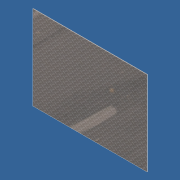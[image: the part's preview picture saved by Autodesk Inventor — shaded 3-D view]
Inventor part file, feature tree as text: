
AUTODESK INVENTOR PART (.ipt)
format: ipt  version: 2012 (Build 160160000, 160)  size: 88,576 bytes
history: native  units: in
note: dims shown in document units (in); Inventor stores cm internally (conversion verified against a paired STEP export)
features: extrude x1, sketch x1
ambient origin geometry x8: Origin, YZ Plane, XZ Plane, XY Plane, X Axis, Y Axis, Z Axis, Center Point
bodies: Solid1 (feature_tree)
feature tree (2):
  extrude  "Extrusion1"  Depth=36.0in
  sketch  "Sketch1"  dims[d0=48.75in d1=36.0in d2=0.1875in d3=0.0in]
